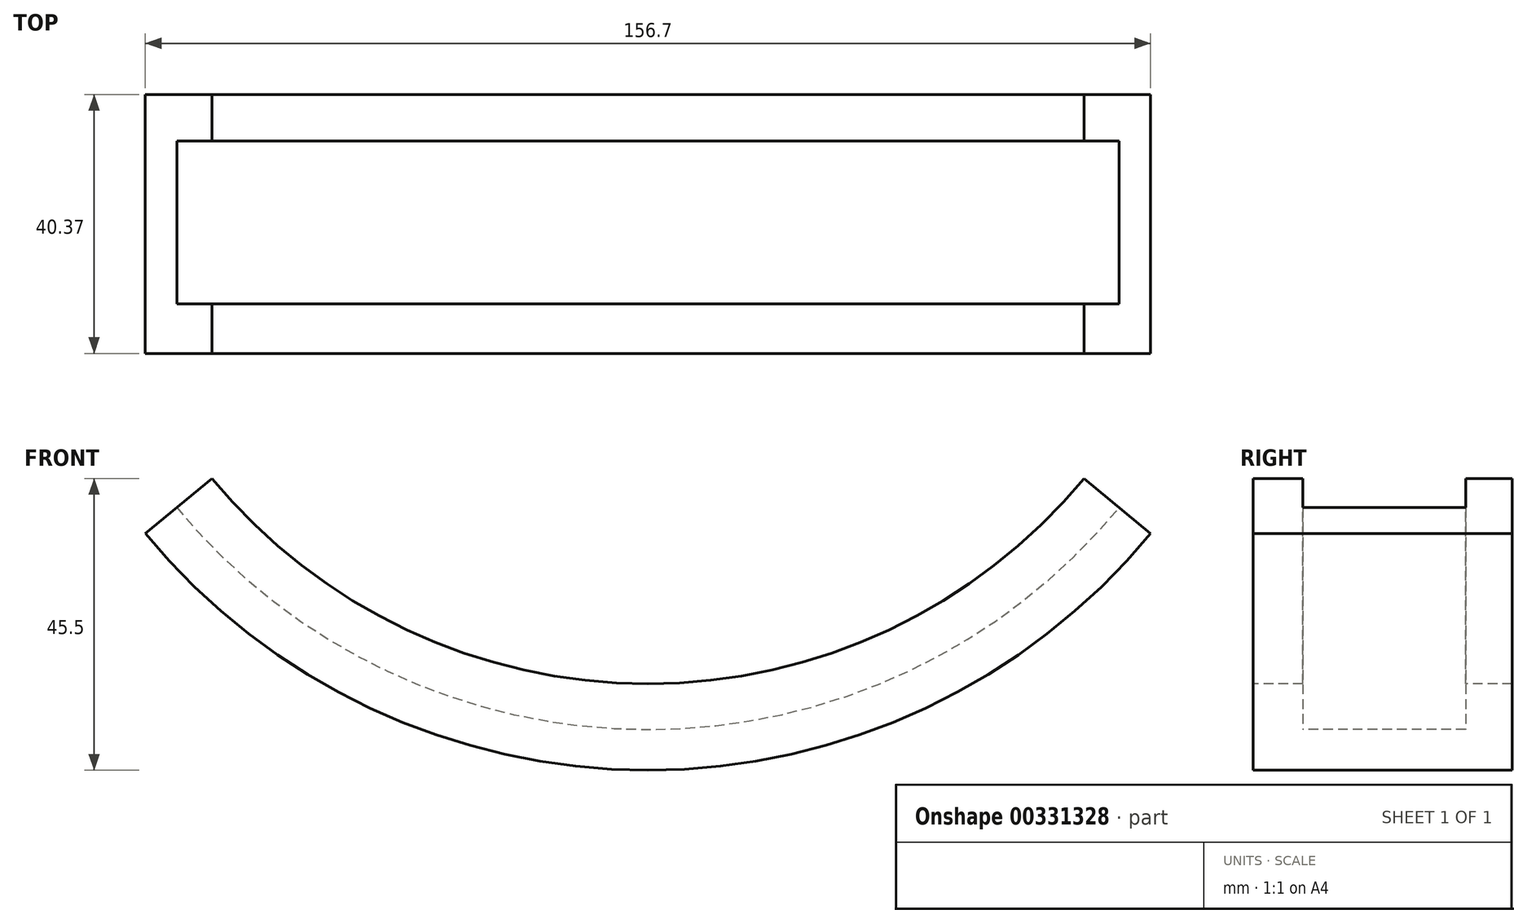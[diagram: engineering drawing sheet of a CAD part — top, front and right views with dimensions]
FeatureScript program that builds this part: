
annotation { "Feature Type Name" : "Feature", "Feature Type Description" : "" }
export const myFeature = defineFeature(function(context is Context, id is Id, definition is map)
    precondition{}
    {
        {
            var Q0;
            Q0=qCreatedBy(makeId("Right.planeOp"),FACE);
            var sketch = newSketch(context, id + "F0", { "sketchPlane" : qUnion([Q0])});
            skLineSegment(sketch, "E0.bottom", {"start": v(0, 0) * mm, "end": v(25.4, 0) * mm});
            skLineSegment(sketch, "E0.top", {"start": v(0, 6.35) * mm, "end": v(25.4, 6.35) * mm});
            skLineSegment(sketch, "E0.left", {"start": v(0, 0) * mm, "end": v(0, 6.35) * mm});
            skLineSegment(sketch, "E0.right", {"start": v(25.4, 0) * mm, "end": v(25.4, 6.35) * mm});
            skLineSegment(sketch, "E1.bottom", {"start": v(0, 0) * mm, "end": v(-7.73, 0) * mm});
            skLineSegment(sketch, "E1.top", {"start": v(0, 13.47) * mm, "end": v(-7.73, 13.47) * mm});
            skLineSegment(sketch, "E1.left", {"start": v(0, 0) * mm, "end": v(0, 13.47) * mm});
            skLineSegment(sketch, "E1.right", {"start": v(-7.73, 0) * mm, "end": v(-7.73, 13.47) * mm});
            skPoint(sketch, "E2.oppositeSnap0", {"position": v(-3.87, 13.47) * mm});
            skLineSegment(sketch, "E2.bottom", {"start": v(25.4, 0) * mm, "end": v(32.64, 0) * mm});
            skLineSegment(sketch, "E2.top", {"start": v(25.4, 13.47) * mm, "end": v(32.64, 13.47) * mm});
            skLineSegment(sketch, "E2.left", {"start": v(25.4, 0) * mm, "end": v(25.4, 13.47) * mm});
            skLineSegment(sketch, "E2.right", {"start": v(32.64, 0) * mm, "end": v(32.64, 13.47) * mm});
            skLineSegment(sketch, "E3", {"start": v(0, 101.6) * mm, "end": v(25.04, 101.6) * mm});
            skSolve(sketch);
        }
        {
            var Q0;
            {var subQ0=sQuery(id+"F0.wireOp",EDGE,"E0.bottom");Q0=makeQuery(id+"F0.imprint","IMPRINT",FACE,{"disambiguationData":[TD([[makeQuery(id+"F0.imprint","IMPRINT",EDGE,{"derivedFrom":subQ0}),1.0]])]});}
            var Q1;
            {var subQ3=sQuery(id+"F0.wireOp",EDGE,"E1.bottom");Q1=makeQuery(id+"F0.imprint","IMPRINT",FACE,{"disambiguationData":[TD([[makeQuery(id+"F0.imprint","IMPRINT",EDGE,{"derivedFrom":subQ3}),-1.0]])]});}
            var Q2;
            {var subQ3=sQuery(id+"F0.wireOp",EDGE,"E2.bottom");Q2=makeQuery(id+"F0.imprint","IMPRINT",FACE,{"disambiguationData":[TD([[makeQuery(id+"F0.imprint","IMPRINT",EDGE,{"derivedFrom":subQ3}),1.0]])]});}
            var Q3;
            Q3=sQuery(id+"F0.wireOp",EDGE,"E3");
            revolve(context, id + "F1", {"entities" : qUnion([Q0, Q1, Q2]), "axis" : qUnion([Q3]), "revolveType" : RevolveType.SYMMETRIC, "angle" : 100.9 * degree});
        }
    });
